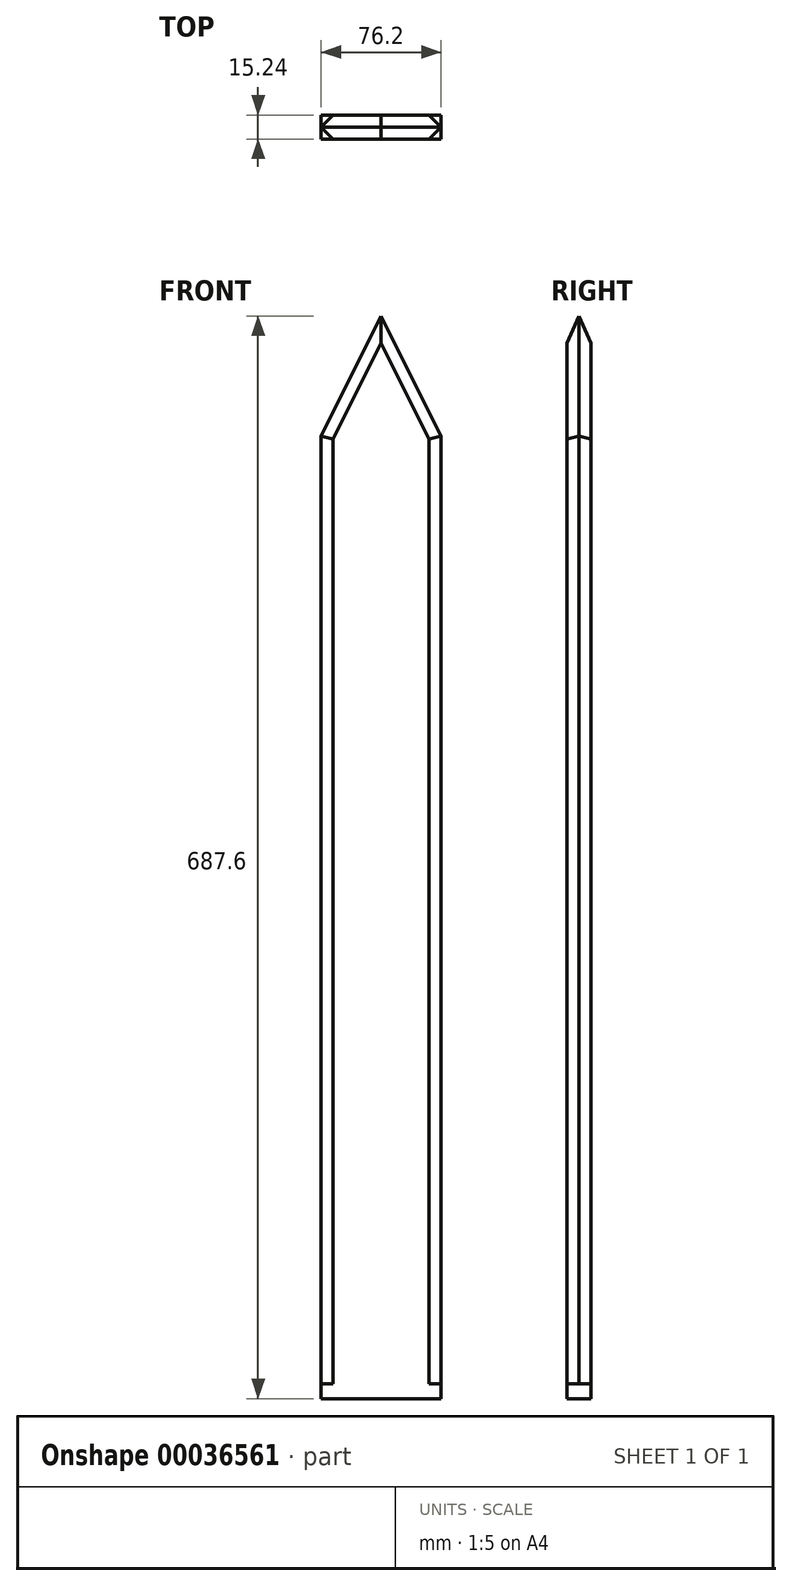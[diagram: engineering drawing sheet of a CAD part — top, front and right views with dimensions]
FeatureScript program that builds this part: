
annotation { "Feature Type Name" : "Feature", "Feature Type Description" : "" }
export const myFeature = defineFeature(function(context is Context, id is Id, definition is map)
    precondition{}
    {
        {
            var Q0;
            Q0=qCreatedBy(makeId("Front.planeOp"),FACE);
            var sketch = newSketch(context, id + "F0", { "sketchPlane" : qUnion([Q0])});
            skLineSegment(sketch, "E0.rect.bottom", {"start": v(38.1, -304.8) * mm, "end": v(-38.1, -304.8) * mm});
            skLineSegment(sketch, "E0.rect.top", {"start": v(38.1, 304.8) * mm, "end": v(-38.1, 304.8) * mm});
            skLineSegment(sketch, "E0.rect.left", {"start": v(38.1, -304.8) * mm, "end": v(38.1, 304.8) * mm});
            skLineSegment(sketch, "E0.rect.right", {"start": v(-38.1, -304.8) * mm, "end": v(-38.1, 304.8) * mm});
            skPoint(sketch, "E0.rect.middle", {"position": v(0, 0) * mm});
            skLineSegment(sketch, "E1", {"start": v(-38.1, 304.8) * mm, "end": v(0, 381) * mm});
            skLineSegment(sketch, "E2", {"start": v(0, 381) * mm, "end": v(38.1, 304.8) * mm});
            skLineSegment(sketch, "E3.bottom", {"start": v(-38.1, -304.8) * mm, "end": v(38.1, -304.8) * mm});
            skLineSegment(sketch, "E3.top", {"start": v(-38.1, 0) * mm, "end": v(38.1, 0) * mm});
            skLineSegment(sketch, "E3.left", {"start": v(-38.1, -304.8) * mm, "end": v(-38.1, 0) * mm});
            skLineSegment(sketch, "E3.right", {"start": v(38.1, -304.8) * mm, "end": v(38.1, 0) * mm});
            skSolve(sketch);
        }
        {
            var Q0;
            Q0 = qSketchRegion(id + "F0", true);
            extrude(context, id + "F1", {"entities" : qUnion([Q0]), "endBound" : BoundingType.SYMMETRIC, "depth" : 15.24 * mm});
        }
        {
            var Q0;
            Q0=makeQuery(id+"F1.opExtrude","CAP_FACE",FACE,{"disambiguationData":[OSD([sQuery(id+"F0.wireOp",EDGE,"E0.rect.bottom"),sQuery(id+"F0.wireOp",EDGE,"E0.rect.left"),sQuery(id+"F0.wireOp",EDGE,"E0.rect.right"),sQuery(id+"F0.wireOp",EDGE,"E1"),sQuery(id+"F0.wireOp",EDGE,"E2")])],"isStart":false});
            var Q1;
            Q1=makeQuery(id+"F1.opExtrude","CAP_FACE",FACE,{"disambiguationData":[OSD([sQuery(id+"F0.wireOp",EDGE,"E0.rect.bottom"),sQuery(id+"F0.wireOp",EDGE,"E0.rect.left"),sQuery(id+"F0.wireOp",EDGE,"E0.rect.right"),sQuery(id+"F0.wireOp",EDGE,"E1"),sQuery(id+"F0.wireOp",EDGE,"E2")])],"isStart":true});
            chamfer(context, id + "F2", {"entities" : qUnion([Q0, Q1]), "width" : 7.62 * mm, "tangentPropagation" : true});
        }
        {
            var Q0;
            Q0=makeQuery(id+"F1.opExtrude","CAP_FACE",FACE,{"disambiguationData":[OSD([sQuery(id+"F0.wireOp",EDGE,"E0.rect.left"),sQuery(id+"F0.wireOp",EDGE,"E0.rect.right"),sQuery(id+"F0.wireOp",EDGE,"E1"),sQuery(id+"F0.wireOp",EDGE,"E2"),sQuery(id+"F0.wireOp",EDGE,"E3.bottom"),sQuery(id+"F0.wireOp",EDGE,"E3.left"),sQuery(id+"F0.wireOp",EDGE,"E3.right")])],"isStart":false});
            var sketch = newSketch(context, id + "F3", { "sketchPlane" : qUnion([Q0])});
            skLineSegment(sketch, "E4.bottom", {"start": v(-38.1, -297.18) * mm, "end": v(38.1, -297.18) * mm});
            skLineSegment(sketch, "E4.top", {"start": v(-38.1, -306.6) * mm, "end": v(38.1, -306.6) * mm});
            skLineSegment(sketch, "E4.left", {"start": v(-38.1, -297.18) * mm, "end": v(-38.1, -306.6) * mm});
            skLineSegment(sketch, "E4.right", {"start": v(38.1, -297.18) * mm, "end": v(38.1, -306.6) * mm});
            skLineSegment(sketch, "E5", {"start": v(0, -297.18) * mm, "end": v(0, 20.15) * mm, "construction": true});
            skSolve(sketch);
        }
        {
            var Q0;
            Q0 = qSketchRegion(id + "F3", true);
            extrude(context, id + "F4", {"entities" : qUnion([Q0]), "operationType" : NewBodyOperationType.ADD, "oppositeDirection" : true, "depth" : 15.24 * mm});
        }
    });
